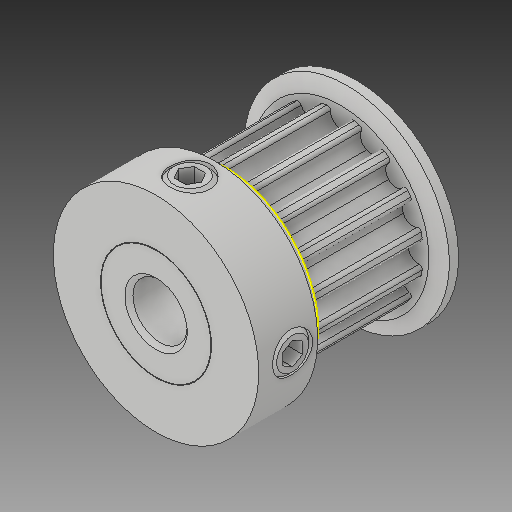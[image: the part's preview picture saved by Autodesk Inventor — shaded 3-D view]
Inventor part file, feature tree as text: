
AUTODESK INVENTOR PART (.ipt)
format: ipt  version: 2019.4 (Build 234330000, 330)  size: 389,120 bytes
history: native  units: mm
features: sketch x1, projected_geometry x1, imported_body x1
ambient origin geometry x8: Origin, YZ Plane, XZ Plane, XY Plane, X Axis, Y Axis, Z Axis, Center Point
bodies: Solid1 (feature_tree)
feature tree (3):
  sketch  "Sketch1"
  projected_geometry  "Projected Loop1"
  imported_body  "Base1"
